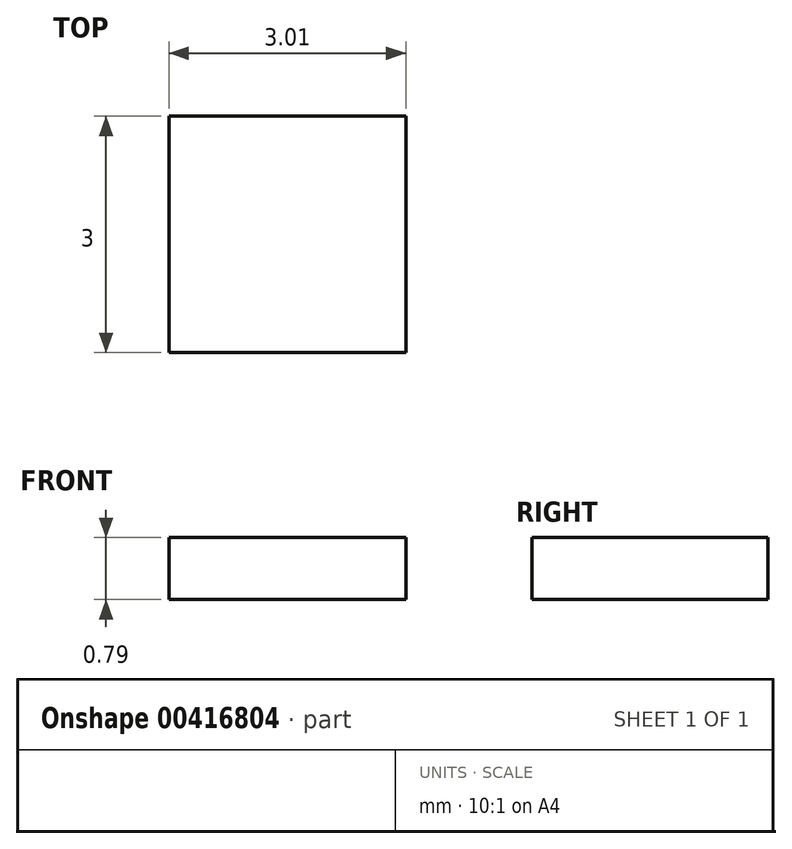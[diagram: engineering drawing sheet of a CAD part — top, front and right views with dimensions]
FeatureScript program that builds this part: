
annotation { "Feature Type Name" : "Feature", "Feature Type Description" : "" }
export const myFeature = defineFeature(function(context is Context, id is Id, definition is map)
    precondition{}
    {
        {
            var Q0;
            Q0=qCreatedBy(makeId("Top.planeOp"),FACE);
            var sketch = newSketch(context, id + "F0", { "sketchPlane" : qUnion([Q0])});
            skLineSegment(sketch, "E0.bottom", {"start": v(0, 0) * mm, "end": v(3, 0) * mm});
            skLineSegment(sketch, "E0.top", {"start": v(0, 3) * mm, "end": v(3, 3) * mm});
            skLineSegment(sketch, "E0.left", {"start": v(0, 0) * mm, "end": v(0, 3) * mm});
            skLineSegment(sketch, "E0.right", {"start": v(3, 0) * mm, "end": v(3, 3) * mm});
            skSolve(sketch);
        }
        {
            var Q0;
            Q0 = qSketchRegion(id + "F0", true);
            extrude(context, id + "F1", {"entities" : qUnion([Q0]), "depth" : .79 * mm, "offsetDistance" : 25.4 * mm});
        }
    });
